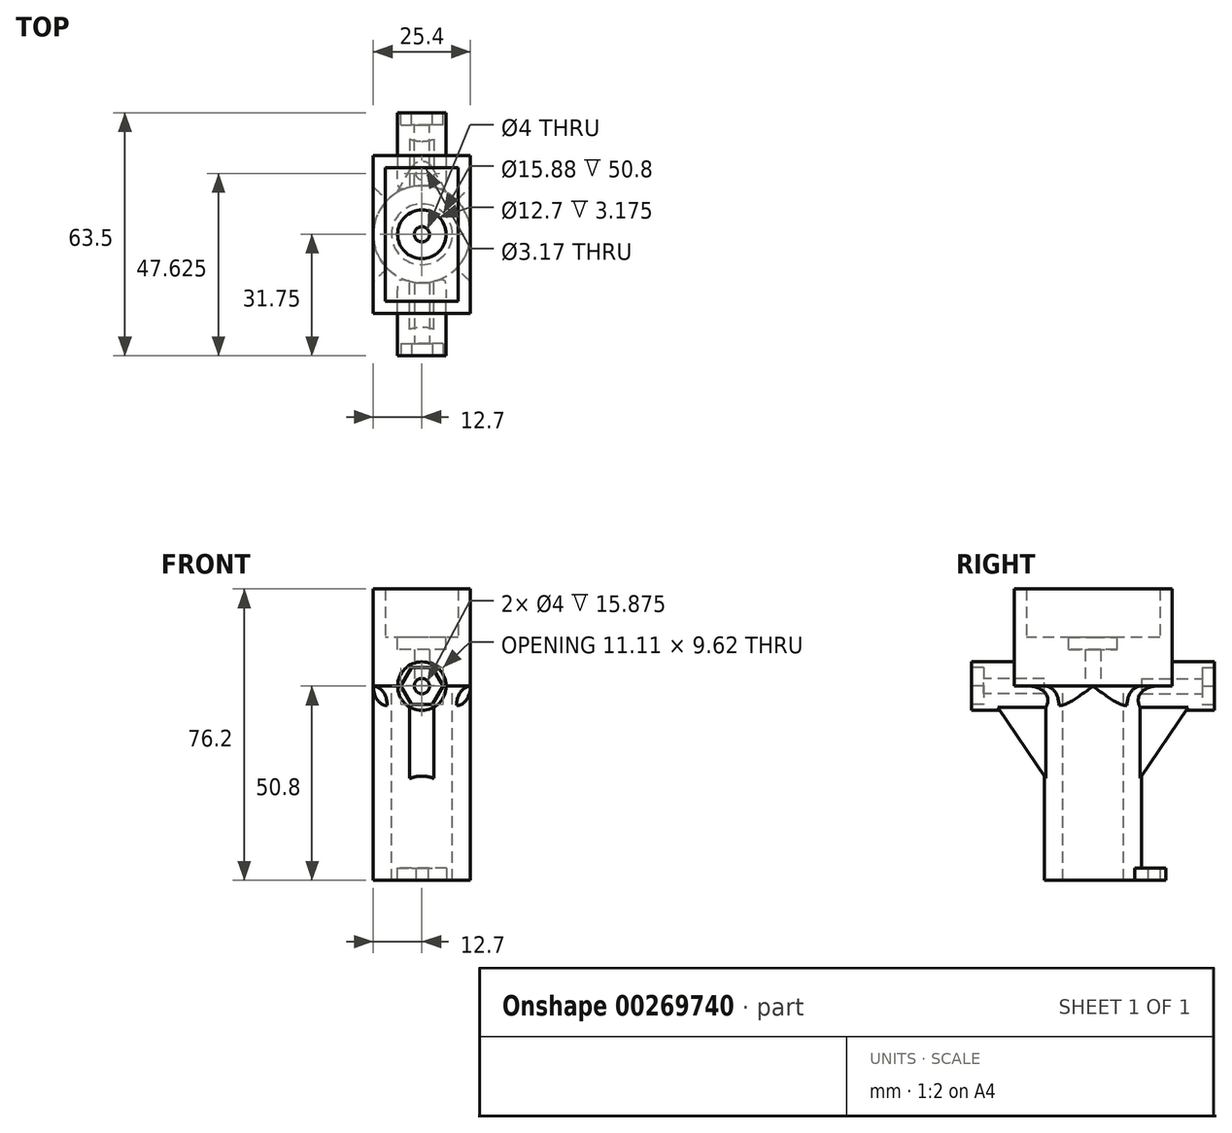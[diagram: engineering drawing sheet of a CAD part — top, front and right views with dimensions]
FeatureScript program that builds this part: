
annotation { "Feature Type Name" : "Feature", "Feature Type Description" : "" }
export const myFeature = defineFeature(function(context is Context, id is Id, definition is map)
    precondition{}
    {
        {
            var Q0;
            Q0=qCreatedBy(makeId("Top.planeOp"),FACE);
            var sketch = newSketch(context, id + "F0", { "sketchPlane" : qUnion([Q0])});
            skCircle(sketch, "E0", {"center": v(0, 0) * mm, "radius": 12.7 * mm});
            skCircle(sketch, "E1", {"center": v(0, 0) * mm, "radius": 7.94 * mm});
            skSolve(sketch);
        }
        {
            var Q0;
            Q0=qSketchRegion(id+"F0",true);
            extrude(context, id + "F1", {"entities" : qUnion([Q0]), "oppositeDirection" : true, "depth" : 50.8 * mm});
        }
        {
            var Q0;
            Q0=qCreatedBy(makeId("Top.planeOp"),FACE);
            var sketch = newSketch(context, id + "F2", { "sketchPlane" : qUnion([Q0])});
            skCircle(sketch, "E2", {"center": v(0, 0) * mm, "radius": 2 * mm});
            skLineSegment(sketch, "E3.bottom", {"start": v(12.7, 20.64) * mm, "end": v(-12.7, 20.64) * mm});
            skLineSegment(sketch, "E3.top", {"start": v(12.7, -20.64) * mm, "end": v(-12.7, -20.64) * mm});
            skLineSegment(sketch, "E3.left", {"start": v(12.7, 20.64) * mm, "end": v(12.7, -20.64) * mm});
            skLineSegment(sketch, "E3.right", {"start": v(-12.7, 20.64) * mm, "end": v(-12.7, -20.64) * mm});
            skSolve(sketch);
        }
        {
            var Q0;
            Q0=qSketchRegion(id+"F2",true);
            extrude(context, id + "F3", {"entities" : qUnion([Q0]), "operationType" : NewBodyOperationType.ADD, "depth" : 12.7 * mm});
        }
        {
            var Q0;
            Q0=qCreatedBy(makeId("Front.planeOp"),FACE);
            var sketch = newSketch(context, id + "F4", { "sketchPlane" : qUnion([Q0])});
            skCircle(sketch, "E4", {"center": v(0, 0) * mm, "radius": 6.35 * mm});
            skSolve(sketch);
        }
        {
            var Q0;
            Q0=qSketchRegion(id+"F4",true);
            extrude(context, id + "F5", {"entities" : qUnion([Q0]), "operationType" : NewBodyOperationType.ADD, "depth" : 31.75 * mm, "hasSecondDirection" : true, "secondDirectionOppositeDirection" : false, "secondDirectionDepth" : 10.16 * mm});
        }
        {
            var Q0;
            Q0=qCreatedBy(makeId("Front.planeOp"),FACE);
            var sketch = newSketch(context, id + "F6", { "sketchPlane" : qUnion([Q0])});
            skCircle(sketch, "E5", {"center": v(0, 0) * mm, "radius": 6.35 * mm});
            skSolve(sketch);
        }
        {
            var Q0;
            Q0=qSketchRegion(id+"F6",true);
            extrude(context, id + "F7", {"entities" : qUnion([Q0]), "operationType" : NewBodyOperationType.ADD, "oppositeDirection" : true, "depth" : 31.75 * mm, "hasSecondDirection" : true, "secondDirectionOppositeDirection" : true, "secondDirectionDepth" : 10.16 * mm});
        }
        {
            var Q0;
            Q0=makeQuery(id+"F5.opExtrude","CAP_FACE",FACE,{"disambiguationData":[OSD([sQuery(id+"F4.wireOp",EDGE,"E4")])],"isStart":false});
            var sketch = newSketch(context, id + "F8", { "sketchPlane" : qUnion([Q0])});
            skCircle(sketch, "E6", {"center": v(0, 0) * mm, "radius": 2 * mm});
            skSolve(sketch);
        }
        {
            var Q0;
            Q0=qSketchRegion(id+"F8",true);
            extrude(context, id + "F9", {"entities" : qUnion([Q0]), "operationType" : NewBodyOperationType.REMOVE, "oppositeDirection" : true, "depth" : 19.05 * mm});
        }
        {
            var Q0;
            Q0=makeQuery(id+"F7.opExtrude","CAP_FACE",FACE,{"disambiguationData":[OSD([sQuery(id+"F6.wireOp",EDGE,"E5")])],"isStart":false});
            var sketch = newSketch(context, id + "F10", { "sketchPlane" : qUnion([Q0])});
            skCircle(sketch, "E7", {"center": v(0, 0) * mm, "radius": 2 * mm});
            skSolve(sketch);
        }
        {
            var Q0;
            Q0=qSketchRegion(id+"F10",true);
            extrude(context, id + "F11", {"entities" : qUnion([Q0]), "operationType" : NewBodyOperationType.REMOVE, "oppositeDirection" : true, "depth" : 19.05 * mm});
        }
        {
            var Q0;
            Q0=makeQuery(id+"F5.opExtrude","CAP_FACE",FACE,{"disambiguationData":[OSD([sQuery(id+"F4.wireOp",EDGE,"E4")])],"isStart":false});
            var sketch = newSketch(context, id + "F12", { "sketchPlane" : qUnion([Q0])});
            skCircle(sketch, "E8.cCircle", {"center": v(0, 0) * mm, "radius": 5.56 * mm, "construction": true});
            skLineSegment(sketch, "E8.0", {"start": v(5.56, 0) * mm, "end": v(2.78, -4.81) * mm});
            skLineSegment(sketch, "E8.1", {"start": v(2.78, -4.81) * mm, "end": v(-2.78, -4.81) * mm});
            skLineSegment(sketch, "E8.2", {"start": v(-2.78, -4.81) * mm, "end": v(-5.56, 0) * mm});
            skLineSegment(sketch, "E8.3", {"start": v(-5.56, 0) * mm, "end": v(-2.78, 4.81) * mm});
            skLineSegment(sketch, "E8.4", {"start": v(-2.78, 4.81) * mm, "end": v(2.78, 4.81) * mm});
            skLineSegment(sketch, "E8.5", {"start": v(2.78, 4.81) * mm, "end": v(5.56, 0) * mm});
            skSolve(sketch);
        }
        {
            var Q0;
            Q0=qSketchRegion(id+"F12",true);
            extrude(context, id + "F13", {"entities" : qUnion([Q0]), "operationType" : NewBodyOperationType.REMOVE, "oppositeDirection" : true, "depth" : 3.17 * mm});
        }
        {
            var Q0;
            Q0=makeQuery(id+"F7.opExtrude","CAP_FACE",FACE,{"disambiguationData":[OSD([sQuery(id+"F6.wireOp",EDGE,"E5")])],"isStart":false});
            var sketch = newSketch(context, id + "F14", { "sketchPlane" : qUnion([Q0])});
            skCircle(sketch, "E9.cCircle", {"center": v(0, 0) * mm, "radius": 5.56 * mm, "construction": true});
            skLineSegment(sketch, "E9.0", {"start": v(5.56, 0) * mm, "end": v(2.78, -4.81) * mm});
            skLineSegment(sketch, "E9.1", {"start": v(2.78, -4.81) * mm, "end": v(-2.78, -4.81) * mm});
            skLineSegment(sketch, "E9.2", {"start": v(-2.78, -4.81) * mm, "end": v(-5.56, 0) * mm});
            skLineSegment(sketch, "E9.3", {"start": v(-5.56, 0) * mm, "end": v(-2.78, 4.81) * mm});
            skLineSegment(sketch, "E9.4", {"start": v(-2.78, 4.81) * mm, "end": v(2.78, 4.81) * mm});
            skLineSegment(sketch, "E9.5", {"start": v(2.78, 4.81) * mm, "end": v(5.56, 0) * mm});
            skSolve(sketch);
        }
        {
            var Q0;
            Q0=qSketchRegion(id+"F14",true);
            extrude(context, id + "F15", {"entities" : qUnion([Q0]), "operationType" : NewBodyOperationType.REMOVE, "oppositeDirection" : true, "depth" : 3.17 * mm});
        }
        {
            var Q0;
            Q0=qCreatedBy(makeId("Right.planeOp"),FACE);
            var sketch = newSketch(context, id + "F16", { "sketchPlane" : qUnion([Q0])});
            skLineSegment(sketch, "E10.left", {"start": v(11.43, -4.76) * mm, "end": v(11.43, -25.4) * mm});
            skLineSegment(sketch, "E10.right", {"start": v(-11.43, -4.76) * mm, "end": v(-11.43, -25.4) * mm});
            skPoint(sketch, "E10.middle", {"position": v(0, 0) * mm});
            skLineSegment(sketch, "E11.top", {"start": v(25.4, -4.76) * mm, "end": v(11.43, -4.76) * mm});
            skLineSegment(sketch, "E12", {"start": v(-25.4, -4.76) * mm, "end": v(-11.43, -25.4) * mm});
            skLineSegment(sketch, "E13", {"start": v(11.43, -25.4) * mm, "end": v(25.4, -4.76) * mm});
            skLineSegment(sketch, "E14.trimOffspring", {"start": v(-11.43, -4.76) * mm, "end": v(-25.4, -4.76) * mm});
            skSolve(sketch);
        }
        {
            var Q0;
            Q0=qSketchRegion(id+"F16",true);
            extrude(context, id + "F17", {"entities" : qUnion([Q0]), "operationType" : NewBodyOperationType.ADD, "endBound" : BoundingType.SYMMETRIC, "depth" : 6.35 * mm});
        }
        {
            var Q0;
            Q0=makeQuery(id+"F3.opExtrude","CAP_FACE",FACE,{"disambiguationData":[OSD([sQuery(id+"F2.wireOp",EDGE,"E2"),sQuery(id+"F2.wireOp",EDGE,"E3.bottom"),sQuery(id+"F2.wireOp",EDGE,"E3.top"),sQuery(id+"F2.wireOp",EDGE,"E3.left"),sQuery(id+"F2.wireOp",EDGE,"E3.right")])],"isStart":false});
            var sketch = newSketch(context, id + "F18", { "sketchPlane" : qUnion([Q0])});
            skLineSegment(sketch, "E15.bottom", {"start": v(12.7, 20.64) * mm, "end": v(-12.7, 20.64) * mm});
            skLineSegment(sketch, "E15.top", {"start": v(12.7, -20.64) * mm, "end": v(-12.7, -20.64) * mm});
            skLineSegment(sketch, "E15.left", {"start": v(12.7, 20.64) * mm, "end": v(12.7, -20.64) * mm});
            skLineSegment(sketch, "E15.right", {"start": v(-12.7, 20.64) * mm, "end": v(-12.7, -20.64) * mm});
            skPoint(sketch, "E15.middle", {"position": v(0, 0) * mm});
            skLineSegment(sketch, "E16.bottom", {"start": v(9.53, 17.46) * mm, "end": v(-9.53, 17.46) * mm});
            skLineSegment(sketch, "E16.top", {"start": v(9.53, -17.46) * mm, "end": v(-9.53, -17.46) * mm});
            skLineSegment(sketch, "E16.left", {"start": v(9.53, 17.46) * mm, "end": v(9.53, -17.46) * mm});
            skLineSegment(sketch, "E16.right", {"start": v(-9.53, 17.46) * mm, "end": v(-9.53, -17.46) * mm});
            skSolve(sketch);
        }
        {
            var Q0;
            Q0=qSketchRegion(id+"F18",true);
            extrude(context, id + "F19", {"entities" : qUnion([Q0]), "operationType" : NewBodyOperationType.ADD, "depth" : 12.7 * mm});
        }
        {
            var Q0;
            Q0=makeQuery(id+"F3.opExtrude","CAP_FACE",FACE,{"disambiguationData":[OSD([sQuery(id+"F2.wireOp",EDGE,"E2"),sQuery(id+"F2.wireOp",EDGE,"E3.bottom"),sQuery(id+"F2.wireOp",EDGE,"E3.top"),sQuery(id+"F2.wireOp",EDGE,"E3.left"),sQuery(id+"F2.wireOp",EDGE,"E3.right")])],"isStart":false});
            var sketch = newSketch(context, id + "F20", { "sketchPlane" : qUnion([Q0])});
            skCircle(sketch, "E17", {"center": v(0, 0) * mm, "radius": 6.35 * mm});
            skSolve(sketch);
        }
        {
            var Q0;
            Q0=qSketchRegion(id+"F20",true);
            extrude(context, id + "F21", {"entities" : qUnion([Q0]), "operationType" : NewBodyOperationType.REMOVE, "oppositeDirection" : true, "depth" : 3.17 * mm});
        }
        {
            var Q0;
            {var subQ0=sQuery(id+"F0.wireOp",EDGE,"E0");var subQ1=sQuery(id+"F2.wireOp",EDGE,"E3.left");Q0=makeQuery(id+"F5.boolean.opBoolean","SPLIT",EDGE,{"disambiguationData":[TD([makeQuery(id+"F3.opExtrude","SWEPT_FACE",FACE,{"disambiguationData":[OSD([subQ1])]})])],"derivedFrom":makeQuery(id+"F3.boolean.opBoolean","SPLIT",EDGE,{"disambiguationData":[OD(1.0)],"derivedFrom":makeQuery(id+"F1.opExtrude","CAP_EDGE",EDGE,{"disambiguationData":[OSD([subQ0])],"isStart":true})})});}
            var Q1;
            {var subQ0=sQuery(id+"F0.wireOp",EDGE,"E0");var subQ1=sQuery(id+"F2.wireOp",EDGE,"E3.right");Q1=makeQuery(id+"F5.boolean.opBoolean","SPLIT",EDGE,{"disambiguationData":[TD([makeQuery(id+"F3.opExtrude","SWEPT_FACE",FACE,{"disambiguationData":[OSD([subQ1])]})])],"derivedFrom":makeQuery(id+"F3.boolean.opBoolean","SPLIT",EDGE,{"disambiguationData":[OD(1.0)],"derivedFrom":makeQuery(id+"F1.opExtrude","CAP_EDGE",EDGE,{"disambiguationData":[OSD([subQ0])],"isStart":true})})});}
            fillet(context, id + "F22", {"entities" : qUnion([Q0, Q1]), "radius" : 5.08 * mm, "tangentPropagation" : true, "allowEdgeOverflow" : false});
        }
        {
            var Q0;
            Q0=makeQuery(id+"F1.opExtrude","CAP_FACE",FACE,{"disambiguationData":[OSD([sQuery(id+"F0.wireOp",EDGE,"E0"),sQuery(id+"F0.wireOp",EDGE,"E1")])],"isStart":false});
            var sketch = newSketch(context, id + "F23", { "sketchPlane" : qUnion([Q0])});
            skPoint(sketch, "E18.orphan", {"position": v(-14.31, 0) * mm});
            skPoint(sketch, "E19.orphan", {"position": v(-6.43, -31.72) * mm});
            skPoint(sketch, "E20.center.orphan", {"position": v(0, -31.72) * mm});
            skArc(sketch, "E21", {"start": v(-2.76, -17.45) * mm, "mid": v(0, -19.05) * mm, "end": v(2.76, -17.45) * mm});
            skLineSegment(sketch, "E22", {"start": v(-6.47, -10.93) * mm, "end": v(-2.76, -17.45) * mm});
            skLineSegment(sketch, "E23", {"start": v(6.47, -10.93) * mm, "end": v(2.76, -17.45) * mm});
            skArc(sketch, "E24", {"start": v(-6.47, -10.93) * mm, "mid": v(0, -12.7) * mm, "end": v(6.47, -10.93) * mm});
            skCircle(sketch, "E25", {"center": v(0, 0) * mm, "radius": 15.88 * mm, "construction": true});
            skLineSegment(sketch, "E26", {"start": v(0, -12.7) * mm, "end": v(-9.53, -12.7) * mm, "construction": true});
            skLineSegment(sketch, "E27", {"start": v(0, -12.7) * mm, "end": v(9.52, -12.7) * mm, "construction": true});
            skLineSegment(sketch, "E28", {"start": v(0, 0) * mm, "end": v(-9.53, -12.7) * mm, "construction": true});
            skLineSegment(sketch, "E29", {"start": v(0, 0) * mm, "end": v(0, -15.88) * mm, "construction": true});
            skCircle(sketch, "E30", {"center": v(0, -15.88) * mm, "radius": 1.59 * mm});
            skSolve(sketch);
        }
        {
            var Q0;
            Q0=qSketchRegion(id+"F23",true);
            extrude(context, id + "F24", {"entities" : qUnion([Q0]), "operationType" : NewBodyOperationType.ADD, "oppositeDirection" : true, "depth" : 3.17 * mm});
        }
    });
